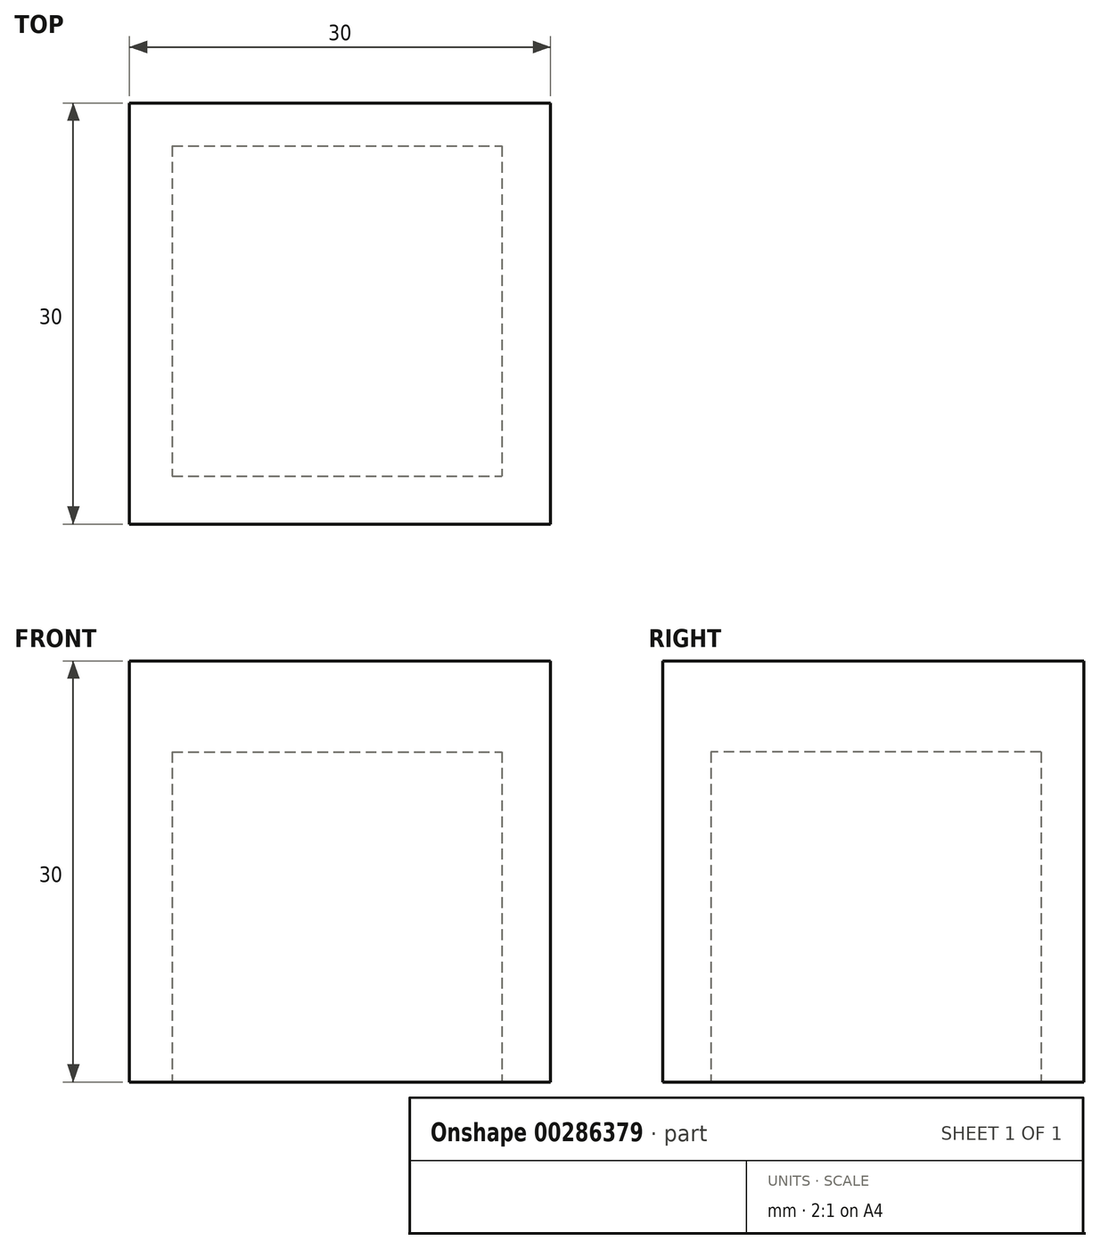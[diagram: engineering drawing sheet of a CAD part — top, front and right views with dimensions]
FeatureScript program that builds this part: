
annotation { "Feature Type Name" : "Feature", "Feature Type Description" : "" }
export const myFeature = defineFeature(function(context is Context, id is Id, definition is map)
    precondition{}
    {
        {
            var Q0;
            Q0=qCreatedBy(makeId("Front.planeOp"),FACE);
            var sketch = newSketch(context, id + "F0", { "sketchPlane" : qUnion([Q0])});
            skLineSegment(sketch, "E0.bottom", {"start": v(0, 0) * mm, "end": v(30, 0) * mm});
            skLineSegment(sketch, "E0.top", {"start": v(0, 30) * mm, "end": v(30, 30) * mm});
            skLineSegment(sketch, "E0.left", {"start": v(0, 0) * mm, "end": v(0, 30) * mm});
            skLineSegment(sketch, "E0.right", {"start": v(30, 0) * mm, "end": v(30, 30) * mm});
            skSolve(sketch);
        }
        {
            var Q0;
            Q0 = qSketchRegion(id + "F0", true);
            extrude(context, id + "F1", {"entities" : qUnion([Q0]), "depth" : 30 * mm});
        }
        {
            var Q0;
            Q0=makeQuery(id+"F1.opExtrude","SWEPT_FACE",FACE,{"disambiguationData":[OSD([sQuery(id+"F0.wireOp",EDGE,"E0.bottom")])]});
            var sketch = newSketch(context, id + "F2", { "sketchPlane" : qUnion([Q0])});
            skLineSegment(sketch, "E1.bottom", {"start": v(3.03, 3.06) * mm, "end": v(26.55, 3.06) * mm});
            skLineSegment(sketch, "E1.top", {"start": v(3.03, 26.57) * mm, "end": v(26.55, 26.57) * mm});
            skLineSegment(sketch, "E1.left", {"start": v(3.03, 3.06) * mm, "end": v(3.03, 26.57) * mm});
            skLineSegment(sketch, "E1.right", {"start": v(26.55, 3.06) * mm, "end": v(26.55, 26.57) * mm});
            skSolve(sketch);
        }
        {
            var Q0;
            Q0 = qSketchRegion(id + "F2", true);
            extrude(context, id + "F3", {"entities" : qUnion([Q0]), "operationType" : NewBodyOperationType.REMOVE, "oppositeDirection" : true, "depth" : 23.51 * mm});
        }
    });
